FCSTD DOCUMENT  (FreeCAD 1.0RUnknown)
Label: wardrobe_corpus02_jan
License: All rights reserved
LicenseURL: https://en.wikipedia.org/wiki/All_rights_reserved
objects: App::FeaturePython×15, App::Link×10, Assembly::JointGroup×1, Assembly::AssemblyObject×1
EXTERNAL_REF file=parts/wardrobe_base_jan.FCStd obj=Body
EXTERNAL_REF file=parts/wardrobe_right_corpus02_jan.FCStd obj=Body002
EXTERNAL_REF file=parts/wardrobe_left_corpus02_jan.FCStd obj=Body001
EXTERNAL_REF file=parts/wardrobe_top_jan.FCStd obj=Body003
EXTERNAL_REF file=parts/wardrobe_backplate_corpus02_jan.FCStd obj=Body004
EXTERNAL_REF file=../purchased parts/hettich-level-adjustment.FCStd obj=Body
EXTERNAL_REF file=parts/wardrobe_door_corpus02_jan.FCStd obj=Body

FEATURE [App::Link] wardrobe_base_jan
  LinkedObject = -> <external parts/wardrobe_base_jan.FCStd>#Body
FEATURE [App::FeaturePython] GroundedJoint  # Assembly grounded joint (typed FeaturePython)
  ObjectToGround = -> wardrobe_base_jan
FEATURE [App::Link] wardrobe_right_jan_corpus00  label="wardrobe_right_corpus02_jan"
  LinkPlacement = pos=(251,-5.11e-14,390) rot=(0,0,1;0rad)
  LinkedObject = -> <external parts/wardrobe_right_corpus02_jan.FCStd>#Body002
  Placement = pos=(251,-5.11e-14,390) rot=(0,0,1;0rad)
FEATURE [App::Link] wardrobe_left_jan_corpus00  label="wardrobe_left_corpus02_jan"
  LinkPlacement = pos=(-270,9.63e-14,390) rot=(0,0,1;0rad)
  LinkedObject = -> <external parts/wardrobe_left_corpus02_jan.FCStd>#Body001
  Placement = pos=(-270,9.63e-14,390) rot=(0,0,1;0rad)
FEATURE [App::Link] wardrobe_top_jan
  LinkPlacement = pos=(-2.095e-13,-1.636e-13,761) rot=(0,0,1;0rad)
  LinkedObject = -> <external parts/wardrobe_top_jan.FCStd>#Body003
  Placement = pos=(-2.095e-13,-1.636e-13,761) rot=(0,0,1;0rad)
FEATURE [App::Link] wardrobe_backplate_jan_corpus00  label="wardrobe_backplate_corpus02_jan"
  LinkPlacement = pos=(-3e-15,300,390) rot=(0,0,1;3.14159rad)
  LinkedObject = -> <external parts/wardrobe_backplate_corpus02_jan.FCStd>#Body004
  Placement = pos=(-3e-15,300,390) rot=(0,0,1;3.14159rad)
FEATURE [App::FeaturePython] Joint002  label="StarrerVerbund002"  # Assembly joint (typed FeaturePython)
  Activated = true
  AngleMax = 0
  AngleMin = 0
  Detach1 = false
  Detach2 = false
  Distance = 0
  Distance2 = 0
  EnableAngleMax = false
  EnableAngleMin = false
  EnableLengthMax = false
  EnableLengthMin = false
  JointType = 0 (Fixed)
  LengthMax = 0
  LengthMin = 0
  Offset2 = pos=(0,0,0) rot=(0,0,1;3.14159rad)
  Placement1 = pos=(-3e-15,0,-390) rot=(0.707107,0,0.707107;3.14159rad)
  Placement2 = pos=(0,300,0) rot=(0,1,0;4.71239rad)
  Reference1 = -> Assembly [wardrobe_backplate_jan_corpus00.Edge3,wardrobe_backplate_jan_corpus00.Edge3]
  Reference2 = -> Assembly [wardrobe_base_jan.Edge9,wardrobe_base_jan.Edge9]
FEATURE [App::FeaturePython] Joint  label="StarrerVerbund"  # Assembly joint (typed FeaturePython)
  Activated = true
  AngleMax = 0
  AngleMin = 0
  Detach1 = false
  Detach2 = false
  Distance = 0
  Distance2 = 0
  EnableAngleMax = false
  EnableAngleMin = false
  EnableLengthMax = false
  EnableLengthMin = false
  JointType = 0 (Fixed)
  LengthMax = 0
  LengthMin = 0
  Placement1 = pos=(19,-1.137e-13,-371) rot=(0.57735,0.57735,0.57735;4.18879rad)
  Placement2 = pos=(270,0,19) rot=(0.57735,0.57735,0.57735;4.18879rad)
  Reference1 = -> Assembly [wardrobe_right_jan_corpus00.Edge4,wardrobe_right_jan_corpus00.Edge4]
  Reference2 = -> Assembly [wardrobe_base_jan.Edge7,wardrobe_base_jan.Edge7]
FEATURE [App::FeaturePython] Joint003  label="StarrerVerbund003"  # Assembly joint (typed FeaturePython)
  Activated = true
  AngleMax = 0
  AngleMin = 0
  Detach1 = false
  Detach2 = false
  Distance = 0
  Distance2 = 0
  EnableAngleMax = false
  EnableAngleMin = false
  EnableLengthMax = false
  EnableLengthMin = false
  JointType = 0 (Fixed)
  LengthMax = 0
  LengthMin = 0
  Offset2 = pos=(0,0,0) rot=(0,0,1;3.14159rad)
  Placement1 = pos=(1.137e-13,-9.63e-14,-371) rot=(0.57735,0.57735,0.57735;4.18879rad)
  Placement2 = pos=(-270,0,19) rot=(-0.57735,0.57735,-0.57735;4.18879rad)
  Reference1 = -> Assembly [wardrobe_left_jan_corpus00.Edge3,wardrobe_left_jan_corpus00.Edge3]
  Reference2 = -> Assembly [wardrobe_base_jan.Edge12,wardrobe_base_jan.Edge12]
FEATURE [App::FeaturePython] Joint004  label="StarrerVerbund004"  # Assembly joint (typed FeaturePython)
  Activated = true
  AngleMax = 0
  AngleMin = 0
  Detach1 = false
  Detach2 = false
  Distance = 0
  Distance2 = 0
  EnableAngleMax = false
  EnableAngleMin = false
  EnableLengthMax = false
  EnableLengthMin = false
  JointType = 0 (Fixed)
  LengthMax = 0
  LengthMin = 0
  Offset2 = pos=(0,0,0) rot=(0,0,1;3.14159rad)
  Placement1 = pos=(270,1.5e-15,0) rot=(0.57735,0.57735,0.57735;4.18879rad)
  Placement2 = pos=(19,1.137e-13,371) rot=(-0.57735,0.57735,-0.57735;4.18879rad)
  Reference1 = -> Assembly [wardrobe_top_jan.Edge6,wardrobe_top_jan.Edge6]
  Reference2 = -> Assembly [wardrobe_right_jan_corpus00.Edge10,wardrobe_right_jan_corpus00.Edge10]
FEATURE [App::Link] hettich_level_adjustment  label="hettich-level-adjustment"
  LinkPlacement = pos=(-218.25,-240,-1.33e-14) rot=(0.707107,0.707107,0;3.14159rad)
  LinkedObject = -> <external ../purchased parts/hettich-level-adjustment.FCStd>#Body
  Placement = pos=(-218.25,-240,-1.33e-14) rot=(0.707107,0.707107,0;3.14159rad)
FEATURE [App::Link] hettich_level_adjustment001  label="hettich-level-adjustment001"
  LinkPlacement = pos=(218.25,-240,-3.9e-15) rot=(-0.707107,0.707107,0;3.14159rad)
  LinkedObject = -> <external ../purchased parts/hettich-level-adjustment.FCStd>#Body
  Placement = pos=(218.25,-240,-3.9e-15) rot=(-0.707107,0.707107,0;3.14159rad)
FEATURE [App::Link] hettich_level_adjustment002  label="hettich-level-adjustment002"
  LinkPlacement = pos=(218.25,240,-1.97e-14) rot=(0.707107,-0.707107,0;3.14159rad)
  LinkedObject = -> <external ../purchased parts/hettich-level-adjustment.FCStd>#Body
  Placement = pos=(218.25,240,-1.97e-14) rot=(0.707107,-0.707107,0;3.14159rad)
FEATURE [App::Link] hettich_level_adjustment003  label="hettich-level-adjustment003"
  LinkPlacement = pos=(-218.25,240,1.33e-14) rot=(0.707107,0.707107,0;3.14159rad)
  LinkedObject = -> <external ../purchased parts/hettich-level-adjustment.FCStd>#Body
  Placement = pos=(-218.25,240,1.33e-14) rot=(0.707107,0.707107,0;3.14159rad)
FEATURE [App::FeaturePython] Joint005  label="StarrerVerbund005"  # Assembly joint (typed FeaturePython)
  Activated = true
  AngleMax = 0
  AngleMin = 0
  Detach1 = false
  Detach2 = false
  Distance = 0
  Distance2 = 0
  EnableAngleMax = false
  EnableAngleMin = false
  EnableLengthMax = false
  EnableLengthMin = false
  JointType = 0 (Fixed)
  LengthMax = 0
  LengthMin = 0
  Offset1 = pos=(0,20,-60) rot=(0,0,1;0rad)
  Placement1 = pos=(-60,-51.75,0) rot=(0.707107,0,0.707107;3.14159rad)
  Placement2 = pos=(-270,-300,0) rot=(-0.57735,-0.57735,0.57735;4.18879rad)
  Reference1 = -> Assembly [hettich_level_adjustment.Edge10,hettich_level_adjustment.Edge10]
  Reference2 = -> Assembly [wardrobe_base_jan.Edge11,wardrobe_base_jan.Vertex1]
FEATURE [App::FeaturePython] Joint006  label="StarrerVerbund006"  # Assembly joint (typed FeaturePython)
  Activated = true
  AngleMax = 0
  AngleMin = 0
  Detach1 = false
  Detach2 = false
  Distance = 0
  Distance2 = 0
  EnableAngleMax = false
  EnableAngleMin = false
  EnableLengthMax = false
  EnableLengthMin = false
  JointType = 0 (Fixed)
  LengthMax = 0
  LengthMin = 0
  Offset1 = pos=(0,-20,60) rot=(0,0,1;0rad)
  Offset2 = pos=(0,0,0) rot=(0,0,1;3.14159rad)
  Placement1 = pos=(250,-240,0) rot=(0.57735,0.57735,0.57735;4.18879rad)
  Placement2 = pos=(0,-31.75,0) rot=(0,-1,0;4.71239rad)
  Reference1 = -> Assembly [wardrobe_base_jan.Edge6,wardrobe_base_jan.Vertex3]
  Reference2 = -> Assembly [hettich_level_adjustment001.Edge10,hettich_level_adjustment001.Edge10]
FEATURE [App::FeaturePython] Joint007  label="StarrerVerbund007"  # Assembly joint (typed FeaturePython)
  Activated = true
  AngleMax = 0
  AngleMin = 0
  Detach1 = false
  Detach2 = false
  Distance = 0
  Distance2 = 0
  EnableAngleMax = false
  EnableAngleMin = false
  EnableLengthMax = false
  EnableLengthMin = false
  JointType = 0 (Fixed)
  LengthMax = 0
  LengthMin = 0
  Offset1 = pos=(0,20,-60) rot=(0,0,1;3.14159rad)
  Placement1 = pos=(-60,-51.75,0) rot=(0,-1,0;4.71239rad)
  Placement2 = pos=(270,300,0) rot=(0.57735,0.57735,0.57735;4.18879rad)
  Reference1 = -> Assembly [hettich_level_adjustment002.Edge10,hettich_level_adjustment002.Edge10]
  Reference2 = -> Assembly [wardrobe_base_jan.Edge6,wardrobe_base_jan.Vertex5]
FEATURE [App::FeaturePython] Joint008  label="StarrerVerbund008"  # Assembly joint (typed FeaturePython)
  Activated = true
  AngleMax = 0
  AngleMin = 0
  Detach1 = false
  Detach2 = false
  Distance = 0
  Distance2 = 0
  EnableAngleMax = false
  EnableAngleMin = false
  EnableLengthMax = false
  EnableLengthMin = false
  JointType = 0 (Fixed)
  LengthMax = 0
  LengthMin = 0
  Offset1 = pos=(0,20,60) rot=(0,0,1;0rad)
  Placement1 = pos=(60,-51.75,0) rot=(0.707107,0,0.707107;3.14159rad)
  Placement2 = pos=(-270,300,0) rot=(-0.57735,-0.57735,0.57735;4.18879rad)
  Reference1 = -> Assembly [hettich_level_adjustment003.Edge10,hettich_level_adjustment003.Edge10]
  Reference2 = -> Assembly [wardrobe_base_jan.Edge11,wardrobe_base_jan.Vertex7]
FEATURE [App::Link] wardrobe_door_corpus02_jan
  LinkPlacement = pos=(267.5,-300,2.1e-15) rot=(1,0,0;1.5708rad)
  LinkedObject = -> <external parts/wardrobe_door_corpus02_jan.FCStd>#Body
  Placement = pos=(267.5,-300,2.1e-15) rot=(1,0,0;1.5708rad)
FEATURE [App::FeaturePython] Joint009  label="Parallel"  # Assembly joint (typed FeaturePython)
  Activated = true
  AngleMax = 0
  AngleMin = 0
  Detach1 = false
  Detach2 = false
  Distance = 0
  Distance2 = 0
  EnableAngleMax = false
  EnableAngleMin = false
  EnableLengthMax = false
  EnableLengthMin = false
  JointType = 6 (Parallel)
  LengthMax = 0
  LengthMin = 0
  Placement1 = pos=(-242.144,565.18,0) rot=(0,0,1;0rad)
  Placement2 = pos=(5.4e-15,-300,9.5) rot=(-1,0,0;1.5708rad)
  Reference1 = -> Assembly [wardrobe_door_corpus02_jan.Face5,wardrobe_door_corpus02_jan.Face5]
  Reference2 = -> Assembly [wardrobe_top_jan.Face1,wardrobe_top_jan.Face1]
FEATURE [App::FeaturePython] Joint010  label="Parallel001"  # Assembly joint (typed FeaturePython)
  Activated = true
  AngleMax = 0
  AngleMin = 0
  Detach1 = false
  Detach2 = false
  Distance = 0
  Distance2 = 0
  EnableAngleMax = false
  EnableAngleMin = false
  EnableLengthMax = false
  EnableLengthMin = false
  JointType = 6 (Parallel)
  LengthMax = 0
  LengthMin = 0
  Placement1 = pos=(0,706.847,9.5) rot=(-0.57735,-0.57735,0.57735;2.0944rad)
  Placement2 = pos=(19,1.018e-13,0) rot=(0.707107,0,0.707107;3.14159rad)
  Reference1 = -> Assembly [wardrobe_door_corpus02_jan.Face1,wardrobe_door_corpus02_jan.Face1]
  Reference2 = -> Assembly [wardrobe_right_jan_corpus00.Face6,wardrobe_right_jan_corpus00.Face6]
FEATURE [App::FeaturePython] Joint011  label="Parallel002"  # Assembly joint (typed FeaturePython)
  Activated = true
  AngleMax = 0
  AngleMin = 0
  Detach1 = false
  Detach2 = false
  Distance = 0
  Distance2 = 0
  EnableAngleMax = false
  EnableAngleMin = false
  EnableLengthMax = false
  EnableLengthMin = false
  JointType = 6 (Parallel)
  LengthMax = 0
  LengthMin = 0
  Placement1 = pos=(-267.5,0,9.5) rot=(0,0.707107,-0.707107;3.14159rad)
  Placement2 = pos=(-1.3e-15,0,0) rot=(0,0,1;0rad)
  Reference1 = -> Assembly [wardrobe_door_corpus02_jan.Face4,wardrobe_door_corpus02_jan.Face4]
  Reference2 = -> Assembly [wardrobe_base_jan.Face5,wardrobe_base_jan.Face5]
FEATURE [App::FeaturePython] Joint012  label="Abstand"  # Assembly joint (typed FeaturePython)
  Activated = true
  AngleMax = 0
  AngleMin = 0
  Detach1 = false
  Detach2 = false
  Distance = 0
  Distance2 = 0
  EnableAngleMax = false
  EnableAngleMin = false
  EnableLengthMax = false
  EnableLengthMin = false
  JointType = 5 (Distance)
  LengthMax = 0
  LengthMin = 0
  Placement1 = pos=(-267.5,0,9.5) rot=(0,0.707107,-0.707107;3.14159rad)
  Placement2 = pos=(-1.3e-15,0,0) rot=(0,0,1;0rad)
  Reference1 = -> Assembly [wardrobe_door_corpus02_jan.Face4,wardrobe_door_corpus02_jan.Face4]
  Reference2 = -> Assembly [wardrobe_base_jan.Face5,wardrobe_base_jan.Face5]
FEATURE [App::FeaturePython] Joint013  label="Abstand001"  # Assembly joint (typed FeaturePython)
  Activated = true
  AngleMax = 0
  AngleMin = 0
  Detach1 = false
  Detach2 = false
  Distance = -2.5
  Distance2 = 0
  EnableAngleMax = false
  EnableAngleMin = false
  EnableLengthMax = false
  EnableLengthMin = false
  JointType = 5 (Distance)
  LengthMax = 0
  LengthMin = 0
  Placement1 = pos=(19,1.018e-13,0) rot=(0.707107,0,0.707107;3.14159rad)
  Placement2 = pos=(0,706.847,9.5) rot=(-0.57735,-0.57735,0.57735;2.0944rad)
  Reference1 = -> Assembly [wardrobe_right_jan_corpus00.Face6,wardrobe_right_jan_corpus00.Vertex2]
  Reference2 = -> Assembly [wardrobe_door_corpus02_jan.Face1,wardrobe_door_corpus02_jan.Face1]
FEATURE [App::FeaturePython] Joint014  label="Abstand002"  # Assembly joint (typed FeaturePython)
  Activated = true
  AngleMax = 0
  AngleMin = 0
  Detach1 = false
  Detach2 = false
  Distance = 0
  Distance2 = 0
  EnableAngleMax = false
  EnableAngleMin = false
  EnableLengthMax = false
  EnableLengthMin = false
  JointType = 5 (Distance)
  LengthMax = 0
  LengthMin = 0
  Placement1 = pos=(-242.144,565.18,0) rot=(0,0,1;0rad)
  Placement2 = pos=(5.4e-15,-300,9.5) rot=(-1,0,0;1.5708rad)
  Reference1 = -> Assembly [wardrobe_door_corpus02_jan.Face5,wardrobe_door_corpus02_jan.Face5]
  Reference2 = -> Assembly [wardrobe_top_jan.Face1,wardrobe_top_jan.Vertex1]
FEATURE [Assembly::JointGroup] Joints
  Group = -> [GroundedJoint,Joint002,Joint,Joint003,Joint004,Joint005,Joint006,Joint007,Joint008,Joint009,Joint010,Joint011,Joint012,Joint013,Joint014]
FEATURE [Assembly::AssemblyObject] Assembly  label="wardrobe_corpus02_jan"
  Group = -> [Joints,wardrobe_base_jan,GroundedJoint,wardrobe_right_jan_corpus00,wardrobe_left_jan_corpus00,wardrobe_top_jan,wardrobe_backplate_jan_corpus00,Joint002,Joint,Joint003,Joint004,hettich_level_adjustment,hettich_level_adjustment001,hettich_level_adjustment002,hettich_level_adjustment003,Joint005,Joint006,Joint007,Joint008,wardrobe_door_corpus02_jan,Joint009,Joint010,Joint011,Joint012,Joint013,+1 more]
  Origin = -> Origin
  Type = Assembly

RESOLVED EXTERNAL PARTS (link-assembly join: the EXTERNAL_REF files above that resolve inside this repo's crawl, each included once):
---- part parts/wardrobe_backplate_corpus02_jan.FCStd = doc fcstd_a9feb5c02d9e ----
FCSTD DOCUMENT  (FreeCAD 1.0RUnknown)
Label: wardrobe_backplate_corpus02_jan
License: All rights reserved
LicenseURL: https://en.wikipedia.org/wiki/All_rights_reserved
objects: Sketcher::SketchObject×1, PartDesign::Pad×1, PartDesign::CoordinateSystem×1, PartDesign::Body×1
note: 7 computed .brp shape members not serialized (recipe doc carries the construction recipe); baked Part::Feature solids carry a one-line shape summary decoded from their .brp
EXTERNAL_REF file=../../mastersketch.FCStd obj=Spreadsheet

FEATURE [Sketcher::SketchObject] Sketch004
  ArcFitTolerance = 1e-06
  AttachmentSupport = -> [XZ_Plane006]
  FullyConstrained = true
  MakeInternals = false
  MapMode = 5
  Placement = pos=(0,0,0) rot=(1,0,0;1.5708rad)
  expr: Constraints[10] = mastersketch#Spreadsheet.corpus_width
  expr: Constraints[11] = mastersketch#Spreadsheet.corpus02_height
  sketch-geometry (5):
    g0: LineSegment StartX=-270 StartY=-390 StartZ=0 EndX=270 EndY=-390 EndZ=0
    g1: LineSegment StartX=270 StartY=-390 StartZ=0 EndX=270 EndY=390 EndZ=0
    g2: LineSegment StartX=270 StartY=390 StartZ=0 EndX=-270 EndY=390 EndZ=0
    g3: LineSegment StartX=-270 StartY=390 StartZ=0 EndX=-270 EndY=-390 EndZ=0
    g4: GeomPoint [constr] X=0 Y=0 Z=0
  constraints (12):
    c: Coincident(g0,g1)
    c: Coincident(g1,g2)
    c: Coincident(g2,g3)
    c: Coincident(g3,g0)
    c: Horizontal(g0)
    c: Horizontal(g2)
    c: Vertical(g1)
    c: Vertical(g3)
    c: Symmetric(g2,g0,g4)
    c: Coincident(g4,g-1)
    c: DistanceX(g0,g0) = 540
    c: DistanceY(g3,g3) = 780
FEATURE [PartDesign::Pad] Pad004
  Direction = (0,-1,2e-16)
  Length = 19
  Length2 = 10
  Placement = pos=(0,0,0) rot=(1,0,0;1.5708rad)
  Profile = -> Sketch004
  ReferenceAxis = -> Sketch004 [N_Axis]
  Refine = true
  Suppressed = false
  Type = 0
  expr: Length = mastersketch#Spreadsheet.corpus_backplate_thickness
FEATURE [PartDesign::CoordinateSystem] LCS_1
  AttacherType = Attacher::AttachEngine3D
  AttachmentSupport = -> [Pad004]
  MapMode = 45
  Placement = pos=(0,-19,-390) rot=(0.57735,0.57735,0.57735;2.0944rad)
FEATURE [PartDesign::Body] Body004  label="wardrobe_backplate_corpus02_jan"
  AllowCompound = false
  Group = -> [Sketch004,Pad004,LCS_1]
  Origin = -> Origin006
  Tip = -> Pad004
---- part parts/wardrobe_base_jan.FCStd = doc fcstd_ceb563eaf676 ----
FCSTD DOCUMENT  (FreeCAD 1.0RUnknown)
Label: wardrobe_base_jan
License: All rights reserved
LicenseURL: https://en.wikipedia.org/wiki/All_rights_reserved
objects: PartDesign::CoordinateSystem×9, Sketcher::SketchObject×2, PartDesign::Pad×1, PartDesign::Body×1
note: 17 computed .brp shape members not serialized (recipe doc carries the construction recipe); baked Part::Feature solids carry a one-line shape summary decoded from their .brp
EXTERNAL_REF file=../../mastersketch.FCStd obj=Spreadsheet

FEATURE [Sketcher::SketchObject] Sketch
  ArcFitTolerance = 1e-06
  AttachmentSupport = -> [XY_Plane]
  FullyConstrained = true
  MakeInternals = false
  MapMode = 5
  expr: Constraints[10] = mastersketch#Spreadsheet.corpus_width
  expr: Constraints[11] = mastersketch#Spreadsheet.corpus_depth
  sketch-geometry (5):
    g0: LineSegment StartX=-270 StartY=-300 StartZ=0 EndX=270 EndY=-300 EndZ=0
    g1: LineSegment StartX=270 StartY=-300 StartZ=0 EndX=270 EndY=300 EndZ=0
    g2: LineSegment StartX=270 StartY=300 StartZ=0 EndX=-270 EndY=300 EndZ=0
    g3: LineSegment StartX=-270 StartY=300 StartZ=0 EndX=-270 EndY=-300 EndZ=0
    g4: GeomPoint [constr] X=0 Y=0 Z=0
  constraints (12):
    c: Coincident(g0,g1)
    c: Coincident(g1,g2)
    c: Coincident(g2,g3)
    c: Coincident(g3,g0)
    c: Horizontal(g0)
    c: Horizontal(g2)
    c: Vertical(g1)
    c: Vertical(g3)
    c: Symmetric(g2,g0,g4)
    c: Coincident(g4,g-1)
    c: DistanceX(g0,g0) = 540
    c: DistanceY(g3,g3) = 600
FEATURE [PartDesign::Pad] Pad
  Direction = (0,0,1)
  Length = 19
  Length2 = 10
  Profile = -> Sketch
  ReferenceAxis = -> Sketch [N_Axis]
  Refine = true
  Suppressed = false
  Type = 0
  expr: Length = mastersketch#Spreadsheet.corpus_outer_thickness
FEATURE [PartDesign::CoordinateSystem] LCS_1  label="LCS_left"
  AttacherType = Attacher::AttachEngine3D
  AttachmentSupport = -> [Pad]
  MapMode = 45
  Placement = pos=(-270,1.42e-14,19) rot=(0,0.707107,0.707107;3.14159rad)
FEATURE [PartDesign::CoordinateSystem] LCS_right  label="LCS-right"
  AttacherType = Attacher::AttachEngine3D
  AttachmentSupport = -> [Pad]
  MapMode = 45
  Placement = pos=(270,-1.42e-14,19) rot=(0,0.707107,0.707107;3.14159rad)
FEATURE [PartDesign::CoordinateSystem] LCS_center
  AttacherType = Attacher::AttachEngine3D
FEATURE [Sketcher::SketchObject] Sketch_1  label="feet_placement"
  ArcFitTolerance = 1e-06
  AttachmentSupport = -> [Pad]
  FullyConstrained = true
  MakeInternals = false
  MapMode = 5
  Placement = pos=(0,0,0) rot=(1,0,0;3.14159rad)
  expr: Constraints[10] = mastersketch#Spreadsheet.corpus_width - 100
  expr: Constraints[11] = mastersketch#Spreadsheet.corpus_depth - 140
  sketch-geometry (5):
    g0: LineSegment StartX=-220 StartY=-230 StartZ=0 EndX=220 EndY=-230 EndZ=0
    g1: LineSegment StartX=220 StartY=-230 StartZ=0 EndX=220 EndY=230 EndZ=0
    g2: LineSegment StartX=220 StartY=230 StartZ=0 EndX=-220 EndY=230 EndZ=0
    g3: LineSegment StartX=-220 StartY=230 StartZ=0 EndX=-220 EndY=-230 EndZ=0
    g4: GeomPoint [constr] X=0 Y=0 Z=0
  constraints (12):
    c: Coincident(g0,g1)
    c: Coincident(g1,g2)
    c: Coincident(g2,g3)
    c: Coincident(g3,g0)
    c: Horizontal(g0)
    c: Horizontal(g2)
    c: Vertical(g1)
    c: Vertical(g3)
    c: Symmetric(g2,g0,g4)
    c: Coincident(g4,g-1)
    c: DistanceX(g0,g0) = 440
    c: DistanceY(g3,g3) = 460
FEATURE [PartDesign::CoordinateSystem] LCS_2  label="LCS_feet0"
  AttacherType = Attacher::AttachEngine3D
  AttachmentSupport = -> [Sketch_1]
  MapMode = 1
  Placement = pos=(-220,-230,0) rot=(0,0,1;0rad)
FEATURE [PartDesign::CoordinateSystem] LCS_feet1
  AttacherType = Attacher::AttachEngine3D
  AttachmentSupport = -> [Sketch_1]
  MapMode = 1
  Placement = pos=(220,-230,0) rot=(0,0,1;0rad)
FEATURE [PartDesign::CoordinateSystem] LCS_feet2
  AttacherType = Attacher::AttachEngine3D
  AttachmentSupport = -> [Sketch_1]
  MapMode = 1
  Placement = pos=(220,230,0) rot=(0,0,1;0rad)
FEATURE [PartDesign::CoordinateSystem] LCS_feet3
  AttacherType = Attacher::AttachEngine3D
  AttachmentSupport = -> [Sketch_1]
  MapMode = 1
  Placement = pos=(-220,230,0) rot=(0,0,1;0rad)
FEATURE [PartDesign::CoordinateSystem] LCS_back
  AttacherType = Attacher::AttachEngine3D
  AttachmentSupport = -> [Pad]
  MapMode = 45
  Placement = pos=(0,300,0) rot=(0.57735,0.57735,0.57735;2.0944rad)
FEATURE [PartDesign::CoordinateSystem] LCS_door
  AttacherType = Attacher::AttachEngine3D
  AttachmentSupport = -> [Pad]
  MapMode = 7
  Placement = pos=(270,-300,0) rot=(0,1,0;3.14159rad)
FEATURE [PartDesign::Body] Body  label="wardrobe_base_jan"
  AllowCompound = false
  Group = -> [Sketch,Pad,LCS_1,LCS_right,LCS_center,Sketch_1,LCS_2,LCS_feet1,LCS_feet2,LCS_feet3,LCS_back,LCS_door]
  Origin = -> Origin
  Tip = -> Pad
---- part parts/wardrobe_door_corpus02_jan.FCStd = doc fcstd_4f2881244b77 ----
FCSTD DOCUMENT  (FreeCAD 1.0R39285 (Git))
Label: wardrobe_door_corpus02_jan
License: All rights reserved
LicenseURL: https://en.wikipedia.org/wiki/All_rights_reserved
objects: TechDraw::DrawViewDimension×5, PartDesign::CoordinateSystem×2, TechDraw::DrawProjGroupItem×2, Sketcher::SketchObject×1, PartDesign::Pad×1, PartDesign::Body×1, TechDraw::DrawSVGTemplate×1, TechDraw::DrawViewAnnotation×1, TechDraw::DrawPage×1, App::Part×1
note: 15 computed .brp shape members not serialized (recipe doc carries the construction recipe); baked Part::Feature solids carry a one-line shape summary decoded from their .brp
EXTERNAL_REF file=../../mastersheet.FCStd obj=Spreadsheet
EXTERNAL_REF file=../../mastersketch.FCStd obj=Sketch

FEATURE [Sketcher::SketchObject] Sketch
  ArcFitTolerance = 1e-06
  AttachmentSupport = -> [XY_Plane]
  FullyConstrained = true
  MakeInternals = false
  MapMode = 5
  expr: Constraints[0] = mastersketch#Sketch.Constraints.corpus02_door_height
  expr: Constraints[10] = mastersketch#Sketch.Constraints.alpha
  expr: Constraints[3] = mastersheet#Spreadsheet.corpus_width - 5
  sketch-geometry (4):
    g0: LineSegment StartX=0 StartY=0 StartZ=0 EndX=0 EndY=1413.69 EndZ=0
    g1: LineSegment StartX=0 StartY=0 StartZ=0 EndX=-535 EndY=0 EndZ=0
    g2: LineSegment StartX=-535 StartY=0 StartZ=0 EndX=-535 EndY=787.688 EndZ=0
    g3: LineSegment StartX=-535 StartY=787.688 StartZ=0 EndX=0 EndY=1413.69 EndZ=0
  constraints (11):
    c: Distance(g0) = 1413.69
    c: Coincident(g0,g-1)
    c: Vertical(g0)
    c: Distance(g1) = 535
    c: Coincident(g1,g0)
    c: PointOnObject(g1,g-1)
    c: Vertical(g2)
    c: Coincident(g3,g2)
    c: Coincident(g2,g1)
    c: Coincident(g3,g0)
    c: Angle(g2,g3) = 2.43442
FEATURE [PartDesign::Pad] Pad
  Direction = (0,0,1)
  Length = 19
  Length2 = 10
  Profile = -> Sketch
  ReferenceAxis = -> Sketch [N_Axis]
  Refine = true
  Suppressed = false
  Type = 0
FEATURE [PartDesign::Body] Body  label="wardrobe_door_corpus02_jan"
  AllowCompound = false
  Group = -> [Sketch,Pad]
  Origin = -> Origin
  Tip = -> Pad
FEATURE [PartDesign::CoordinateSystem] LCS_1
  AttacherType = Attacher::AttachEngine3D
  AttachmentSupport = -> [Pad]
  MapMode = 7
  Placement = pos=(0,0,0) rot=(1,0,0;1.5708rad)
FEATURE [TechDraw::DrawSVGTemplate] Template  label="Vorlage"
  Height = 210
  Orientation = 1
  Template = <userpath>/scoop/apps/freecad/current/data/Mod/TechDraw/Templates/A4_Landscape_TD.svg
  Width = 297
FEATURE [TechDraw::DrawProjGroupItem] View
  CoarseView = false
  Direction = (0,1e-16,-1)
  Focus = 100
  HardHidden = false
  IsoCount = 0
  IsoHidden = false
  IsoVisible = false
  LockPosition = false
  Perspective = false
  Rotation = 0
  RotationVector = (1,0,0)
  Scale = 0.1
  ScaleType = 2
  ScrubCount = 1
  SeamHidden = false
  SeamVisible = false
  SmoothHidden = false
  SmoothVisible = true
  Source = -> [Body]
  Type = 0
  X = 139.755
  XDirection = (-1e-16,-1,-1e-16)
  Y = 148.199
FEATURE [TechDraw::DrawProjGroupItem] View001
  CoarseView = false
  Direction = (-1,-1e-16,0)
  Focus = 100
  HardHidden = false
  IsoCount = 0
  IsoHidden = false
  IsoVisible = false
  LockPosition = false
  Perspective = false
  Rotation = 0
  RotationVector = (1,0,0)
  Scale = 0.1
  ScaleType = 2
  ScrubCount = 1
  SeamHidden = false
  SeamVisible = false
  SmoothHidden = false
  SmoothVisible = true
  Source = -> [Body]
  Type = 0
  X = 139.755
  XDirection = (1e-16,-1,0)
  Y = 90.1338
FEATURE [TechDraw::DrawViewDimension] Dimension  label="Maß"
  AngleOverride = false
  Arbitrary = false
  ArbitraryTolerances = false
  BoxCorners = (2) [(-70.6847,-26.75,0),(70.6847,26.75,0)]
  EqualTolerance = true
  ExtensionAngle = 0
  FormatSpec = %.1w
  FormatSpecOverTolerance = %+.1w
  FormatSpecUnderTolerance = %+.1w
  Inverted = false
  LineAngle = 0
  LockPosition = false
  MeasureType = 1
  OverTolerance = 0
  References2D = -> [View]
  Rotation = 0
  ScaleType = 0
  TheoreticalExact = false
  Type = 1
  UnderTolerance = 0
  X = 0
  Y = -33.1734
FEATURE [TechDraw::DrawViewDimension] Dimension001  label="Maß001"
  AngleOverride = false
  Arbitrary = false
  ArbitraryTolerances = false
  BoxCorners = (2) [(-70.6847,-26.75,0),(70.6847,26.75,0)]
  EqualTolerance = true
  ExtensionAngle = 0
  FormatSpec = %.1w
  FormatSpecOverTolerance = %+.1w
  FormatSpecUnderTolerance = %+.1w
  Inverted = false
  LineAngle = 0
  LockPosition = false
  MeasureType = 1
  OverTolerance = 0
  References2D = -> [View]
  Rotation = 0
  ScaleType = 0
  TheoreticalExact = false
  Type = 2
  UnderTolerance = 0
  X = 76.0797
  Y = 0
FEATURE [TechDraw::DrawViewDimension] Dimension002  label="Maß002"
  AngleOverride = false
  Arbitrary = false
  ArbitraryTolerances = false
  BoxCorners = (2) [(-70.6847,-26.75,0),(70.6847,26.75,0)]
  EqualTolerance = true
  ExtensionAngle = 0
  FormatSpec = %.1w
  FormatSpecOverTolerance = %+.1w
  FormatSpecUnderTolerance = %+.1w
  Inverted = false
  LineAngle = 0
  LockPosition = false
  MeasureType = 1
  OverTolerance = 0
  References2D = -> [View]
  Rotation = 0
  ScaleType = 0
  TheoreticalExact = false
  Type = 1
  UnderTolerance = 0
  X = 31.3003
  Y = 43.1168
FEATURE [TechDraw::DrawViewDimension] Dimension003  label="Maß003"
  AngleOverride = false
  Arbitrary = false
  ArbitraryTolerances = false
  BoxCorners = (2) [(-70.6847,-0.95,0),(70.6847,0.95,0)]
  EqualTolerance = true
  ExtensionAngle = 0
  FormatSpec = %.1w
  FormatSpecOverTolerance = %+.1w
  FormatSpecUnderTolerance = %+.1w
  Inverted = false
  LineAngle = 0
  LockPosition = false
  MeasureType = 1
  OverTolerance = 0
  References2D = -> [View001]
  Rotation = 0
  ScaleType = 0
  TheoreticalExact = false
  Type = 0
  UnderTolerance = 0
  X = 76.6584
  Y = -13.0761
FEATURE [TechDraw::DrawViewDimension] Dimension004  label="Maß004"
  AngleOverride = false
  Arbitrary = false
  ArbitraryTolerances = false
  BoxCorners = (2) [(-70.6847,-26.75,0),(70.6847,26.75,0)]
  EqualTolerance = true
  ExtensionAngle = 0
  FormatSpec = (%.1w)
  FormatSpecOverTolerance = %+.1w
  FormatSpecUnderTolerance = %+.1w
  Inverted = false
  LineAngle = 0
  LockPosition = false
  MeasureType = 1
  OverTolerance = 0
  References2D = -> [View]
  Rotation = 0
  ScaleType = 0
  TheoreticalExact = false
  Type = 6
  UnderTolerance = 0
  X = -0.468348
  Y = 10.2378
FEATURE [TechDraw::DrawViewAnnotation] Annotation  label="Beschriftung"
  Font = MS Shell Dlg 2
  LineSpace = 100
  LockPosition = false
  MaxWidth = -1
  Rotation = 0
  ScaleType = 0
  Text = Artikelnummer: 12391882 oder 6754673
  TextSize = 5
  TextStyle = 0
  X = 208.828
  Y = 61.9887
FEATURE [TechDraw::DrawPage] Page  label="Seite"
  KeepUpdated = true
  NextBalloonIndex = 1
  ProjectionType = 0
  Template = -> Template
  Views = -> [View,View001,Dimension,Dimension001,Dimension002,Dimension003,Dimension004,Annotation]
FEATURE [PartDesign::CoordinateSystem] LCS_Origin
  AttacherType = Attacher::AttachEngine3D
  AttachmentSupport = -> [X_Axis001]
  MapMode = 2
FEATURE [App::Part] wardrobe_door_corpus02_jan  label="wardrobe_door_corpus02_jan001"
  DrawingName = wardrobe_door_corpus02_jan.FCStd
  Group = -> [LCS_Origin,LCS_1,Body]
  Origin = -> Origin001
  PartDescription = wardrobe_door_corpus02_jan
  PartID = wardrobe_door_corpus02_jan
---- part parts/wardrobe_left_corpus02_jan.FCStd = doc fcstd_423097661b1a ----
FCSTD DOCUMENT  (FreeCAD 1.0RUnknown)
Label: wardrobe_left_corpus02_jan
License: All rights reserved
LicenseURL: https://en.wikipedia.org/wiki/All_rights_reserved
objects: PartDesign::CoordinateSystem×3, Sketcher::SketchObject×1, PartDesign::Pad×1, PartDesign::Body×1
note: 9 computed .brp shape members not serialized (recipe doc carries the construction recipe); baked Part::Feature solids carry a one-line shape summary decoded from their .brp
EXTERNAL_REF file=../../mastersketch.FCStd obj=Spreadsheet

FEATURE [Sketcher::SketchObject] Sketch001
  ArcFitTolerance = 1e-06
  AttachmentSupport = -> [YZ_Plane001]
  FullyConstrained = true
  MakeInternals = false
  MapMode = 5
  Placement = pos=(0,0,0) rot=(0.57735,0.57735,0.57735;2.0944rad)
  expr: Constraints[10] = mastersketch#Spreadsheet.corpus_depth
  expr: Constraints[11] = mastersketch#Spreadsheet.corpus02_height - 2 * mastersketch#Spreadsheet.corpus_outer_thickness
  sketch-geometry (5):
    g0: LineSegment StartX=-300 StartY=-371 StartZ=0 EndX=300 EndY=-371 EndZ=0
    g1: LineSegment StartX=300 StartY=-371 StartZ=0 EndX=300 EndY=371 EndZ=0
    g2: LineSegment StartX=300 StartY=371 StartZ=0 EndX=-300 EndY=371 EndZ=0
    g3: LineSegment StartX=-300 StartY=371 StartZ=0 EndX=-300 EndY=-371 EndZ=0
    g4: GeomPoint [constr] X=0 Y=0 Z=0
  constraints (12):
    c: Coincident(g0,g1)
    c: Coincident(g1,g2)
    c: Coincident(g2,g3)
    c: Coincident(g3,g0)
    c: Horizontal(g0)
    c: Horizontal(g2)
    c: Vertical(g1)
    c: Vertical(g3)
    c: Symmetric(g2,g0,g4)
    c: Coincident(g4,g-1)
    c: DistanceX(g0,g0) = 600
    c: DistanceY(g3,g3) = 742
FEATURE [PartDesign::Pad] Pad001
  Direction = (1,0,0)
  Length = 19
  Length2 = 10
  Placement = pos=(0,0,0) rot=(1,1,1;2.0944rad)
  Profile = -> Sketch001
  ReferenceAxis = -> Sketch001 [N_Axis]
  Refine = true
  Suppressed = false
  Type = 0
  expr: Length = mastersketch#Spreadsheet.corpus_outer_thickness
FEATURE [PartDesign::CoordinateSystem] LCS_1  label="LCS_bottom"
  AttacherType = Attacher::AttachEngine3D
  AttachmentSupport = -> [Pad001]
  MapMode = 45
  Placement = pos=(0,-1.42e-14,-371) rot=(0,0.707107,0.707107;3.14159rad)
FEATURE [PartDesign::CoordinateSystem] LCS_top
  AttacherType = Attacher::AttachEngine3D
  AttachmentSupport = -> [Pad001]
  MapMode = 45
  Placement = pos=(0,1.42e-14,371) rot=(0,0.707107,0.707107;3.14159rad)
FEATURE [PartDesign::CoordinateSystem] LCS_inner
  AttacherType = Attacher::AttachEngine3D
  AttachmentSupport = -> [Pad001]
  MapMode = 45
  Placement = pos=(19,-1.82e-14,-371) rot=(0,0.707107,0.707107;3.14159rad)
FEATURE [PartDesign::Body] Body001  label="wardrobe_left_corpus02_jan"
  AllowCompound = false
  Group = -> [Sketch001,Pad001,LCS_1,LCS_top,LCS_inner]
  Origin = -> Origin001
  Tip = -> Pad001
---- part parts/wardrobe_right_corpus02_jan.FCStd = doc fcstd_cb6eb086236d ----
FCSTD DOCUMENT  (FreeCAD 1.0RUnknown)
Label: wardrobe_right_corpus02_jan
License: All rights reserved
LicenseURL: https://en.wikipedia.org/wiki/All_rights_reserved
objects: Sketcher::SketchObject×1, PartDesign::Pad×1, PartDesign::CoordinateSystem×1, PartDesign::Body×1
note: 7 computed .brp shape members not serialized (recipe doc carries the construction recipe); baked Part::Feature solids carry a one-line shape summary decoded from their .brp
EXTERNAL_REF file=../../mastersketch.FCStd obj=Spreadsheet

FEATURE [Sketcher::SketchObject] Sketch002
  ArcFitTolerance = 1e-06
  AttachmentSupport = -> [YZ_Plane004]
  FullyConstrained = true
  MakeInternals = false
  MapMode = 5
  Placement = pos=(0,0,0) rot=(0.57735,0.57735,0.57735;2.0944rad)
  expr: Constraints[10] = mastersketch#Spreadsheet.corpus_depth
  expr: Constraints[11] = mastersketch#Spreadsheet.corpus02_height - 2 * mastersketch#Spreadsheet.corpus_outer_thickness
  sketch-geometry (5):
    g0: LineSegment StartX=-300 StartY=-371 StartZ=0 EndX=300 EndY=-371 EndZ=0
    g1: LineSegment StartX=300 StartY=-371 StartZ=0 EndX=300 EndY=371 EndZ=0
    g2: LineSegment StartX=300 StartY=371 StartZ=0 EndX=-300 EndY=371 EndZ=0
    g3: LineSegment StartX=-300 StartY=371 StartZ=0 EndX=-300 EndY=-371 EndZ=0
    g4: GeomPoint [constr] X=0 Y=0 Z=0
  constraints (12):
    c: Coincident(g0,g1)
    c: Coincident(g1,g2)
    c: Coincident(g2,g3)
    c: Coincident(g3,g0)
    c: Horizontal(g0)
    c: Horizontal(g2)
    c: Vertical(g1)
    c: Vertical(g3)
    c: Symmetric(g2,g0,g4)
    c: Coincident(g4,g-1)
    c: DistanceX(g0,g0) = 600
    c: DistanceY(g3,g3) = 742
FEATURE [PartDesign::Pad] Pad002
  Direction = (1,0,0)
  Length = 19
  Length2 = 10
  Placement = pos=(0,0,0) rot=(1,1,1;2.0944rad)
  Profile = -> Sketch002
  ReferenceAxis = -> Sketch002 [N_Axis]
  Refine = true
  Suppressed = false
  Type = 0
  expr: Length = mastersketch#Spreadsheet.corpus_outer_thickness
FEATURE [PartDesign::CoordinateSystem] LCS_1
  AttacherType = Attacher::AttachEngine3D
  AttachmentSupport = -> [Pad002]
  MapMode = 45
  Placement = pos=(19,-1.82e-14,-371) rot=(0,0.707107,0.707107;3.14159rad)
FEATURE [PartDesign::Body] Body002  label="wardrobe_right_corpus02_jan"
  AllowCompound = false
  Group = -> [Sketch002,Pad002,LCS_1]
  Origin = -> Origin004
  Tip = -> Pad002
---- part parts/wardrobe_top_jan.FCStd = doc fcstd_5a1df6a9867d ----
FCSTD DOCUMENT  (FreeCAD 1.0RUnknown)
Label: wardrobe_top_jan
License: All rights reserved
LicenseURL: https://en.wikipedia.org/wiki/All_rights_reserved
objects: Sketcher::SketchObject×1, PartDesign::Pad×1, PartDesign::CoordinateSystem×1, PartDesign::Body×1
note: 7 computed .brp shape members not serialized (recipe doc carries the construction recipe); baked Part::Feature solids carry a one-line shape summary decoded from their .brp
EXTERNAL_REF file=../../mastersketch.FCStd obj=Spreadsheet

FEATURE [Sketcher::SketchObject] Sketch003
  ArcFitTolerance = 1e-06
  AttachmentSupport = -> [XY_Plane005]
  FullyConstrained = true
  MakeInternals = false
  MapMode = 5
  expr: Constraints[10] = mastersketch#Spreadsheet.corpus_width
  expr: Constraints[11] = mastersketch#Spreadsheet.corpus_depth
  sketch-geometry (5):
    g0: LineSegment StartX=-270 StartY=-300 StartZ=0 EndX=270 EndY=-300 EndZ=0
    g1: LineSegment StartX=270 StartY=-300 StartZ=0 EndX=270 EndY=300 EndZ=0
    g2: LineSegment StartX=270 StartY=300 StartZ=0 EndX=-270 EndY=300 EndZ=0
    g3: LineSegment StartX=-270 StartY=300 StartZ=0 EndX=-270 EndY=-300 EndZ=0
    g4: GeomPoint [constr] X=0 Y=0 Z=0
  constraints (12):
    c: Coincident(g0,g1)
    c: Coincident(g1,g2)
    c: Coincident(g2,g3)
    c: Coincident(g3,g0)
    c: Horizontal(g0)
    c: Horizontal(g2)
    c: Vertical(g1)
    c: Vertical(g3)
    c: Symmetric(g2,g0,g4)
    c: Coincident(g4,g-1)
    c: DistanceX(g0,g0) = 540
    c: DistanceY(g3,g3) = 600
FEATURE [PartDesign::Pad] Pad003
  Direction = (0,0,1)
  Length = 19
  Length2 = 10
  Profile = -> Sketch003
  ReferenceAxis = -> Sketch003 [N_Axis]
  Refine = true
  Suppressed = false
  Type = 0
  expr: Length = mastersketch#Spreadsheet.corpus_outer_thickness
FEATURE [PartDesign::CoordinateSystem] LCS_left
  AttacherType = Attacher::AttachEngine3D
  AttachmentSupport = -> [Pad003]
  MapMode = 45
  Placement = pos=(-270,1.42e-14,0) rot=(0,0.707107,0.707107;3.14159rad)
FEATURE [PartDesign::Body] Body003  label="wardrobe_top_jan"
  AllowCompound = false
  Group = -> [Sketch003,Pad003,LCS_left]
  Origin = -> Origin005
  Tip = -> Pad003
